# Revit family: FU_Table_Sandler_Cono 4001 D36
name_source: partatom
category: Furniture
units: mm (PartAtom-declared; Revit-internal decimal feet)

## family parameters
Always vertical = Yes
Cut with Voids When Loaded = No
OmniClass Number = 23.40.20.00
OmniClass Title = General Furniture and Specialties
Render Appearance Source = Family Geometry
Room Calculation Point = No
Shared = No
Work Plane-Based = No

## types (1)
- Cono 4001 - D36
    Default Elevation = 0 mm  [stored 0 ft]
    Depth = 450 mm  [stored 1.47638 ft]
    Description = Dining table with metal base. 90cm/36"-diameter table top in a woodgrain or lacquered finish, with a reverse knife edge profile. 75cm/29.5" high. Other top profiles/materials available by special request.
    Height = 720 mm  [stored 2.3622 ft]
    Manufacturer = Sandler
    Model = Cono 4001 D36
    Top Type = FU_Top_Sandler_EF125 : 125EF Top 90dia
    URL = https://www.sandlerseating.com
    Width = 450 mm  [stored 1.47638 ft]

note: [stored X ft] marks values corroborated as IEEE doubles in the binary element streams (Revit-internal decimal feet)

## geometry (parser evidence)
native form markers: Sweep x9
no freeform markers — native parametric forms only
